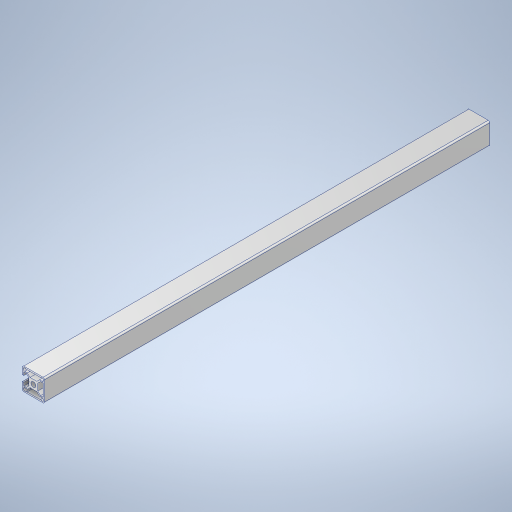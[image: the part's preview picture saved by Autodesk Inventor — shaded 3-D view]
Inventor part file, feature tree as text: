
AUTODESK INVENTOR PART (.ipt)
format: ipt  version: 2024 (Build 280153000, 153)  size: 372,736 bytes
history: native  units: mm
features: other x21, sketch x4, extrude x3, thread x2, hole x1
ambient origin geometry x8: Origin, YZ Plane, XZ Plane, XY Plane, X Axis, Y Axis, Z Axis, Center Point
bodies: Solid1 (feature_tree)
feature tree (31):
  extrude  "Extrusion1"  Depth=600.0mm TaperAngle=0.0deg
  hole  "Hole1"  [1 undecoded]
  extrude  "Extrusion2"  TaperAngle=0.0deg  [1 undecoded]
  extrude  "Extrusion3"  Depth=10.0mm TaperAngle=0.0deg
  other  "C1_XY"
  other  "C1_YZ"
  other  "C1_ZX"
  other  "C1_X"
  other  "C1_Y"
  other  "C1_Z"
  other  "C1_Center"
  other  "to_frame_cap1_XY"
  other  "to_frame_cap1_YZ"
  other  "to_frame_cap1_ZX"
  other  "to_frame_cap1_X"
  other  "to_frame_cap1_Y"
  other  "to_frame_cap1_Z"
  other  "to_frame_cap1_Center"
  other  "to_frame_cap2_XY"
  other  "to_frame_cap2_YZ"
  other  "to_frame_cap2_ZX"
  other  "to_frame_cap2_X"
  other  "to_frame_cap2_Y"
  other  "to_frame_cap2_Z"
  other  "to_frame_cap2_Center"
  thread  "Thread1"  [1 undecoded]
  thread  "Thread2"  [1 undecoded]
  sketch  "Sketch_122"  dims[d2=6.8mm d3=6.0mm d4=4.0mm d5=2.0mm d6=90.0deg d7=600.0mm d8=0.0mm d9=600.0mm d10=0.0mm]
  sketch  "Sketch2"  dims[d0=600.0mm d1=0.0mm]
  sketch  "Sketch_173"  dims[d11=600.0mm d12=0.0mm d13=0.0mm]
  sketch  "Sketch_174"  dims[d14=0.0mm d15=0.0mm d16=10.0mm d17=0.0mm d18=10.0mm d19=0.0mm]
note: 4 required parameter values undecoded (feature->parameter linkage not recoverable at this tier; creation-order binding heuristic only, values carry confidence <= 0.55)
